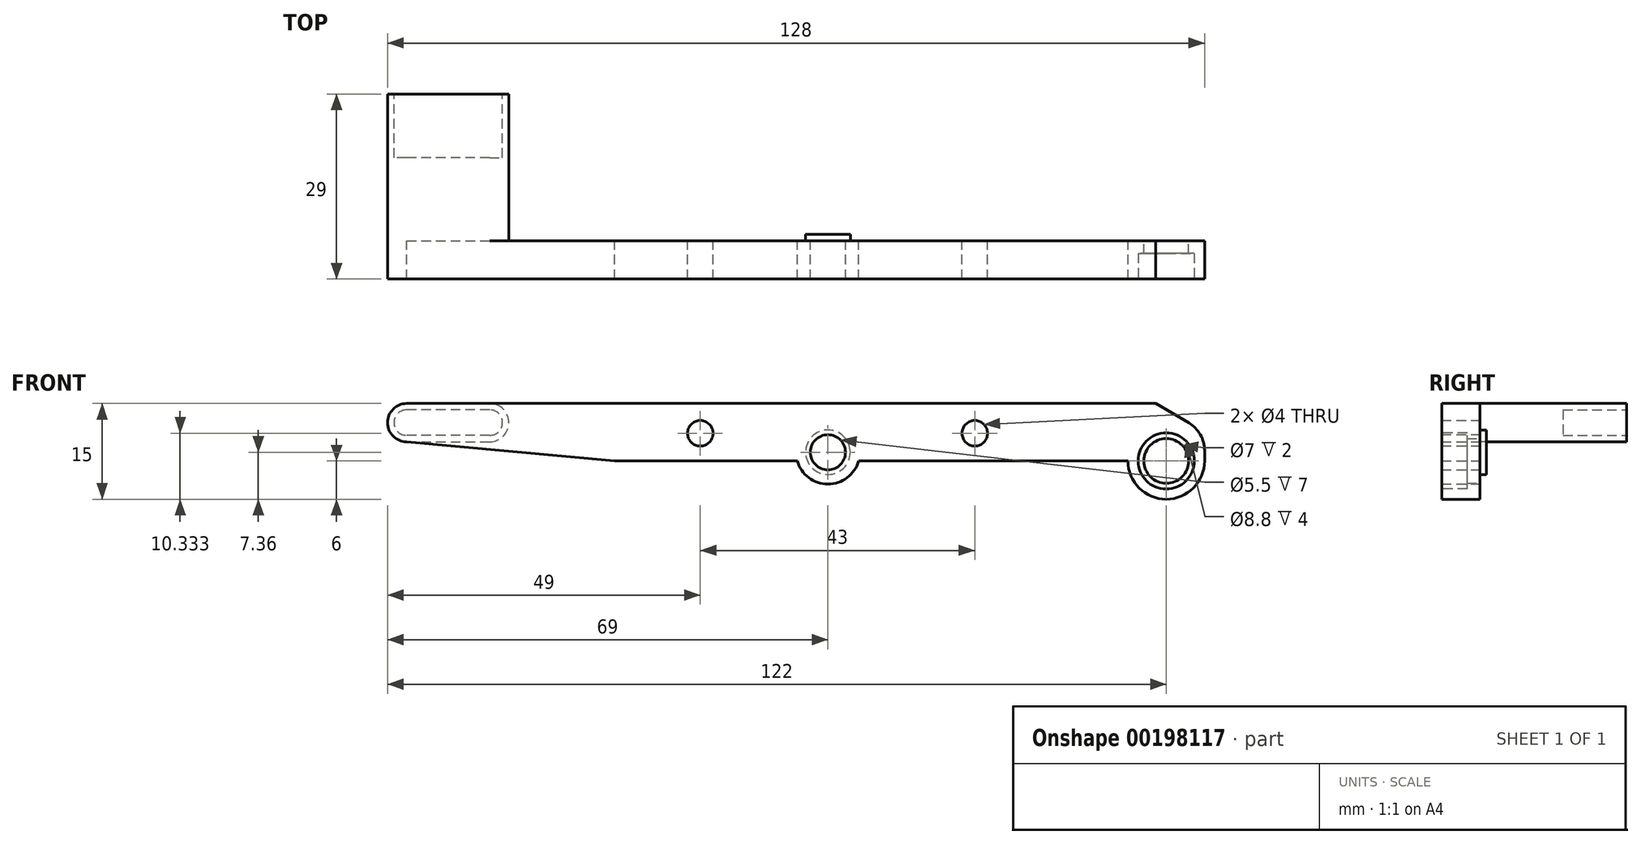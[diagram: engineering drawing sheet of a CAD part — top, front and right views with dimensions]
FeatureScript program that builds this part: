
annotation { "Feature Type Name" : "Feature", "Feature Type Description" : "" }
export const myFeature = defineFeature(function(context is Context, id is Id, definition is map)
    precondition{}
    {
        {
            var Q0;
            Q0=qCreatedBy(makeId("Front.planeOp"),FACE);
            var sketch = newSketch(context, id + "F0", { "sketchPlane" : qUnion([Q0])});
            skLineSegment(sketch, "E0.bottom", {"start": v(32.55, 0) * mm, "end": v(125, 0) * mm});
            skLineSegment(sketch, "E0.top", {"start": v(0, 9) * mm, "end": v(117.37, 9) * mm});
            skLineSegment(sketch, "E0.left", {"start": v(0, 3) * mm, "end": v(0, 9) * mm});
            skLineSegment(sketch, "E0.right", {"start": v(125, 0) * mm, "end": v(125, 1.64) * mm});
            skArc(sketch, "E1", {"start": v(113, 0) * mm, "mid": v(119, -6) * mm, "end": v(125, 0) * mm});
            skCircle(sketch, "E2", {"center": v(119, 0) * mm, "radius": 3.5 * mm});
            skArc(sketch, "E3", {"start": v(61.19, 0) * mm, "mid": v(66, -3.64) * mm, "end": v(70.81, 0) * mm});
            skCircle(sketch, "E4", {"center": v(66, 1.36) * mm, "radius": 2.75 * mm});
            skCircle(sketch, "E5", {"center": v(89, 4.33) * mm, "radius": 2 * mm});
            skCircle(sketch, "E6", {"center": v(46, 4.33) * mm, "radius": 2 * mm});
            skLineSegment(sketch, "E7", {"start": v(117.37, 9) * mm, "end": v(122.54, 5.95) * mm});
            skPoint(sketch, "E8.orphan", {"position": v(125, 9) * mm});
            skLineSegment(sketch, "E9", {"start": v(0, 3) * mm, "end": v(32.55, 0) * mm});
            skPoint(sketch, "E10.orphan", {"position": v(0, 0) * mm});
            skPoint(sketch, "E11.visualSharp", {"position": v(125, 4.5) * mm});
            skArc(sketch, "E11.filletArc", {"start": v(125, 1.64) * mm, "mid": v(124.34, 4.12) * mm, "end": v(122.54, 5.95) * mm});
            skArc(sketch, "E12", {"start": v(0, 9) * mm, "mid": v(-3, 6) * mm, "end": v(0, 3) * mm});
            skSolve(sketch);
        }
        {
            var Q0;
            Q0=qSketchRegion(id+"F0",true);
            extrude(context, id + "F1", {"entities" : qUnion([Q0]), "depth" : 6 * mm});
        }
        {
            var Q0;
            Q0=makeQuery(id+"F1.opExtrude","CAP_FACE",FACE,{"disambiguationData":[OSD([sQuery(id+"F0.wireOp",EDGE,"E0.bottom"),sQuery(id+"F0.wireOp",EDGE,"E0.top"),sQuery(id+"F0.wireOp",EDGE,"E0.right"),sQuery(id+"F0.wireOp",EDGE,"E1"),sQuery(id+"F0.wireOp",EDGE,"E2"),sQuery(id+"F0.wireOp",EDGE,"E3"),sQuery(id+"F0.wireOp",EDGE,"E4"),sQuery(id+"F0.wireOp",EDGE,"E5"),sQuery(id+"F0.wireOp",EDGE,"E6"),sQuery(id+"F0.wireOp",EDGE,"E7"),sQuery(id+"F0.wireOp",EDGE,"E9"),sQuery(id+"F0.wireOp",EDGE,"E11.filletArc"),sQuery(id+"F0.wireOp",EDGE,"E12")])],"isStart":true});
            var sketch = newSketch(context, id + "F2", { "sketchPlane" : qUnion([Q0])});
            skCircle(sketch, "E13", {"center": v(-66, 1.36) * mm, "radius": 2.75 * mm});
            skCircle(sketch, "E14", {"center": v(-66, 1.36) * mm, "radius": 3.5 * mm});
            skSolve(sketch);
        }
        {
            var Q0;
            Q0=qSketchRegion(id+"F2",true);
            extrude(context, id + "F3", {"entities" : qUnion([Q0]), "operationType" : NewBodyOperationType.ADD, "depth" : 1 * mm});
        }
        {
            var Q0;
            Q0=makeQuery(id+"F1.opExtrude","CAP_FACE",FACE,{"disambiguationData":[OSD([sQuery(id+"F0.wireOp",EDGE,"E0.bottom"),sQuery(id+"F0.wireOp",EDGE,"E0.top"),sQuery(id+"F0.wireOp",EDGE,"E0.right"),sQuery(id+"F0.wireOp",EDGE,"E1"),sQuery(id+"F0.wireOp",EDGE,"E2"),sQuery(id+"F0.wireOp",EDGE,"E3"),sQuery(id+"F0.wireOp",EDGE,"E4"),sQuery(id+"F0.wireOp",EDGE,"E5"),sQuery(id+"F0.wireOp",EDGE,"E6"),sQuery(id+"F0.wireOp",EDGE,"E7"),sQuery(id+"F0.wireOp",EDGE,"E9"),sQuery(id+"F0.wireOp",EDGE,"E11.filletArc"),sQuery(id+"F0.wireOp",EDGE,"E12")])],"isStart":false});
            var sketch = newSketch(context, id + "F4", { "sketchPlane" : qUnion([Q0])});
            skCircle(sketch, "E15", {"center": v(119, 0) * mm, "radius": 4.4 * mm});
            skSolve(sketch);
        }
        {
            var Q0;
            Q0 = qSketchRegion(id + "F4", true);
            extrude(context, id + "F5", {"entities" : qUnion([Q0]), "operationType" : NewBodyOperationType.REMOVE, "oppositeDirection" : true, "depth" : 4 * mm});
        }
        {
            var Q0;
            Q0=makeQuery(id+"F1.opExtrude","CAP_FACE",FACE,{"disambiguationData":[OSD([sQuery(id+"F0.wireOp",EDGE,"E0.bottom"),sQuery(id+"F0.wireOp",EDGE,"E0.top"),sQuery(id+"F0.wireOp",EDGE,"E0.right"),sQuery(id+"F0.wireOp",EDGE,"E1"),sQuery(id+"F0.wireOp",EDGE,"E2"),sQuery(id+"F0.wireOp",EDGE,"E3"),sQuery(id+"F0.wireOp",EDGE,"E4"),sQuery(id+"F0.wireOp",EDGE,"E5"),sQuery(id+"F0.wireOp",EDGE,"E6"),sQuery(id+"F0.wireOp",EDGE,"E7"),sQuery(id+"F0.wireOp",EDGE,"E9"),sQuery(id+"F0.wireOp",EDGE,"E11.filletArc"),sQuery(id+"F0.wireOp",EDGE,"E12")])],"isStart":true});
            var sketch = newSketch(context, id + "F6", { "sketchPlane" : qUnion([Q0])});
            skArc(sketch, "E16", {"start": v(0, 3) * mm, "mid": v(3, 6) * mm, "end": v(0, 9) * mm});
            skLineSegment(sketch, "E17.bottom", {"start": v(0, 3) * mm, "end": v(-13, 3) * mm});
            skLineSegment(sketch, "E17.top", {"start": v(0, 9) * mm, "end": v(-13, 9) * mm});
            skLineSegment(sketch, "E17.left", {"start": v(0, 3) * mm, "end": v(0, 9) * mm});
            skLineSegment(sketch, "E17.right", {"start": v(-13, 3) * mm, "end": v(-13, 9) * mm});
            skArc(sketch, "E18", {"start": v(-13, 9) * mm, "mid": v(-16, 6) * mm, "end": v(-13, 3) * mm});
            skSolve(sketch);
        }
        {
            var Q0;
            Q0 = qSketchRegion(id + "F6", true);
            extrude(context, id + "F7", {"entities" : qUnion([Q0]), "operationType" : NewBodyOperationType.ADD, "depth" : 23 * mm});
        }
        {
            var Q0;
            Q0=makeQuery(id+"F7.opExtrude","CAP_FACE",FACE,{"disambiguationData":[OSD([sQuery(id+"F6.wireOp",EDGE,"E16"),sQuery(id+"F6.wireOp",EDGE,"E17.bottom"),sQuery(id+"F6.wireOp",EDGE,"E17.top"),sQuery(id+"F6.wireOp",EDGE,"E18")])],"isStart":false});
            var sketch = newSketch(context, id + "F8", { "sketchPlane" : qUnion([Q0])});
            skArc(sketch, "E19.0", {"start": v(-13, 8) * mm, "mid": v(-15, 6) * mm, "end": v(-13, 4) * mm});
            skArc(sketch, "E20.0", {"start": v(0, 8) * mm, "mid": v(2, 6) * mm, "end": v(0, 4) * mm});
            skLineSegment(sketch, "E21", {"start": v(-13, 8) * mm, "end": v(0, 8) * mm});
            skLineSegment(sketch, "E22", {"start": v(-13, 4) * mm, "end": v(0, 4) * mm});
            skSolve(sketch);
        }
        {
            var Q0;
            Q0 = qSketchRegion(id + "F8", true);
            extrude(context, id + "F9", {"entities" : qUnion([Q0]), "operationType" : NewBodyOperationType.REMOVE, "oppositeDirection" : true, "depth" : 10 * mm});
        }
    });
